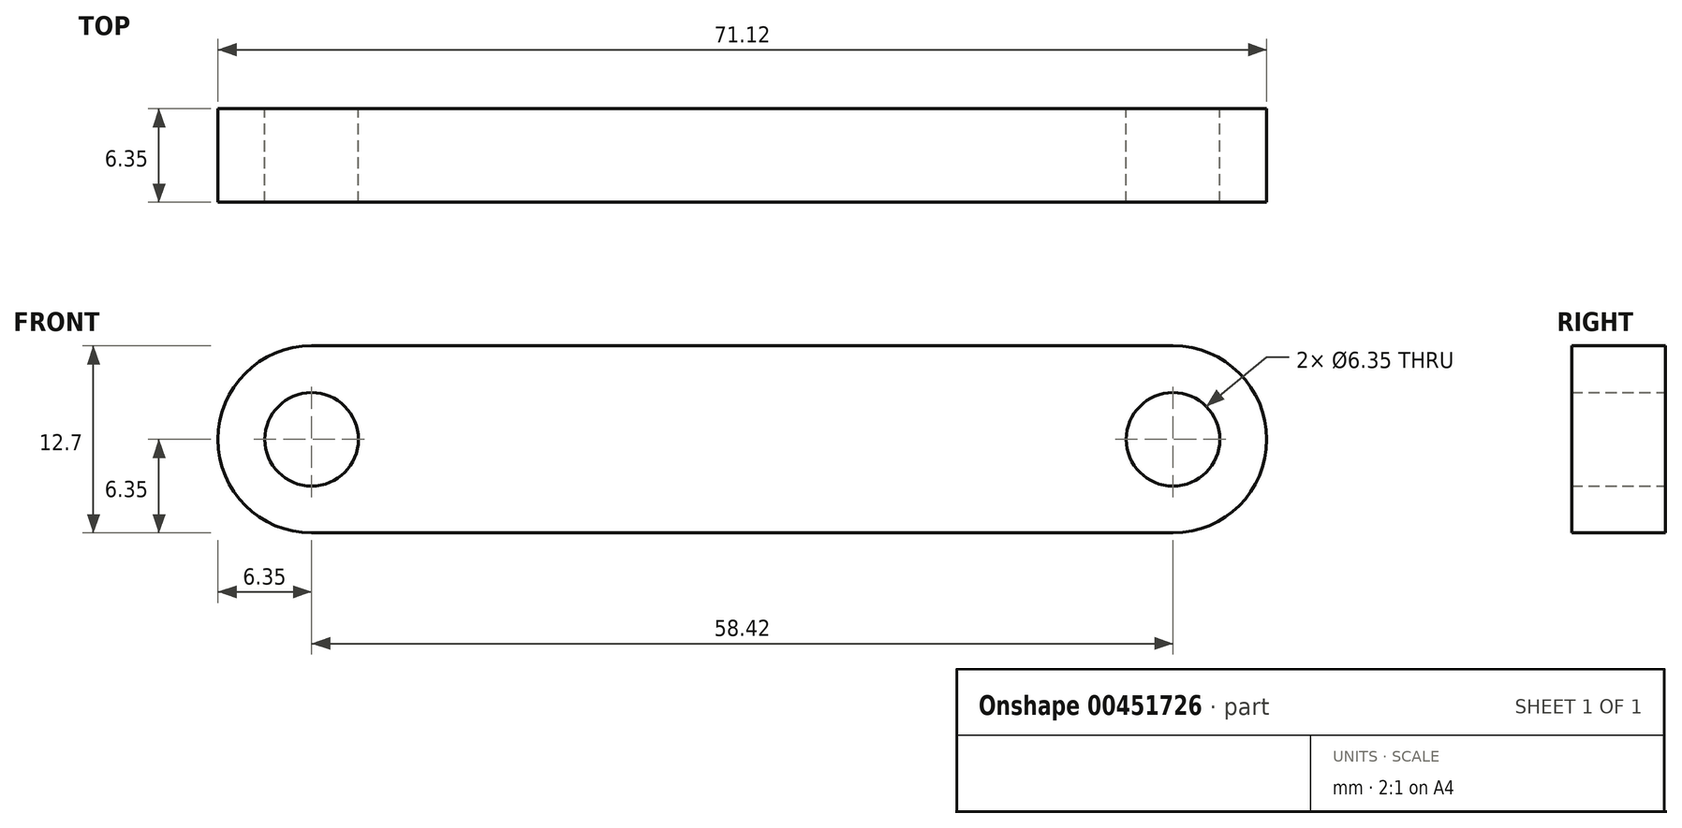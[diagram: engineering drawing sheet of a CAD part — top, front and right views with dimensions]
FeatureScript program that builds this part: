
annotation { "Feature Type Name" : "Feature", "Feature Type Description" : "" }
export const myFeature = defineFeature(function(context is Context, id is Id, definition is map)
    precondition{}
    {
        {
            var Q0;
            Q0=qCreatedBy(makeId("Front.planeOp"),FACE);
            var sketch = newSketch(context, id + "F0", { "sketchPlane" : qUnion([Q0])});
            skArc(sketch, "E0", {"start": v(-29.21, 6.35) * mm, "mid": v(-35.56, 0) * mm, "end": v(-29.21, -6.35) * mm});
            skArc(sketch, "E1", {"start": v(29.21, -6.35) * mm, "mid": v(35.56, 0) * mm, "end": v(29.21, 6.35) * mm});
            skLineSegment(sketch, "E2", {"start": v(-29.21, 6.35) * mm, "end": v(29.21, 6.35) * mm});
            skLineSegment(sketch, "E3", {"start": v(-29.21, -6.35) * mm, "end": v(29.21, -6.35) * mm});
            skCircle(sketch, "E4", {"center": v(-29.21, 0) * mm, "radius": 3.18 * mm});
            skCircle(sketch, "E5", {"center": v(29.21, 0) * mm, "radius": 3.18 * mm});
            skSolve(sketch);
        }
        {
            var Q0;
            Q0 = qSketchRegion(id + "F0", true);
            extrude(context, id + "F1", {"entities" : qUnion([Q0]), "depth" : 6.35 * mm});
        }
    });
